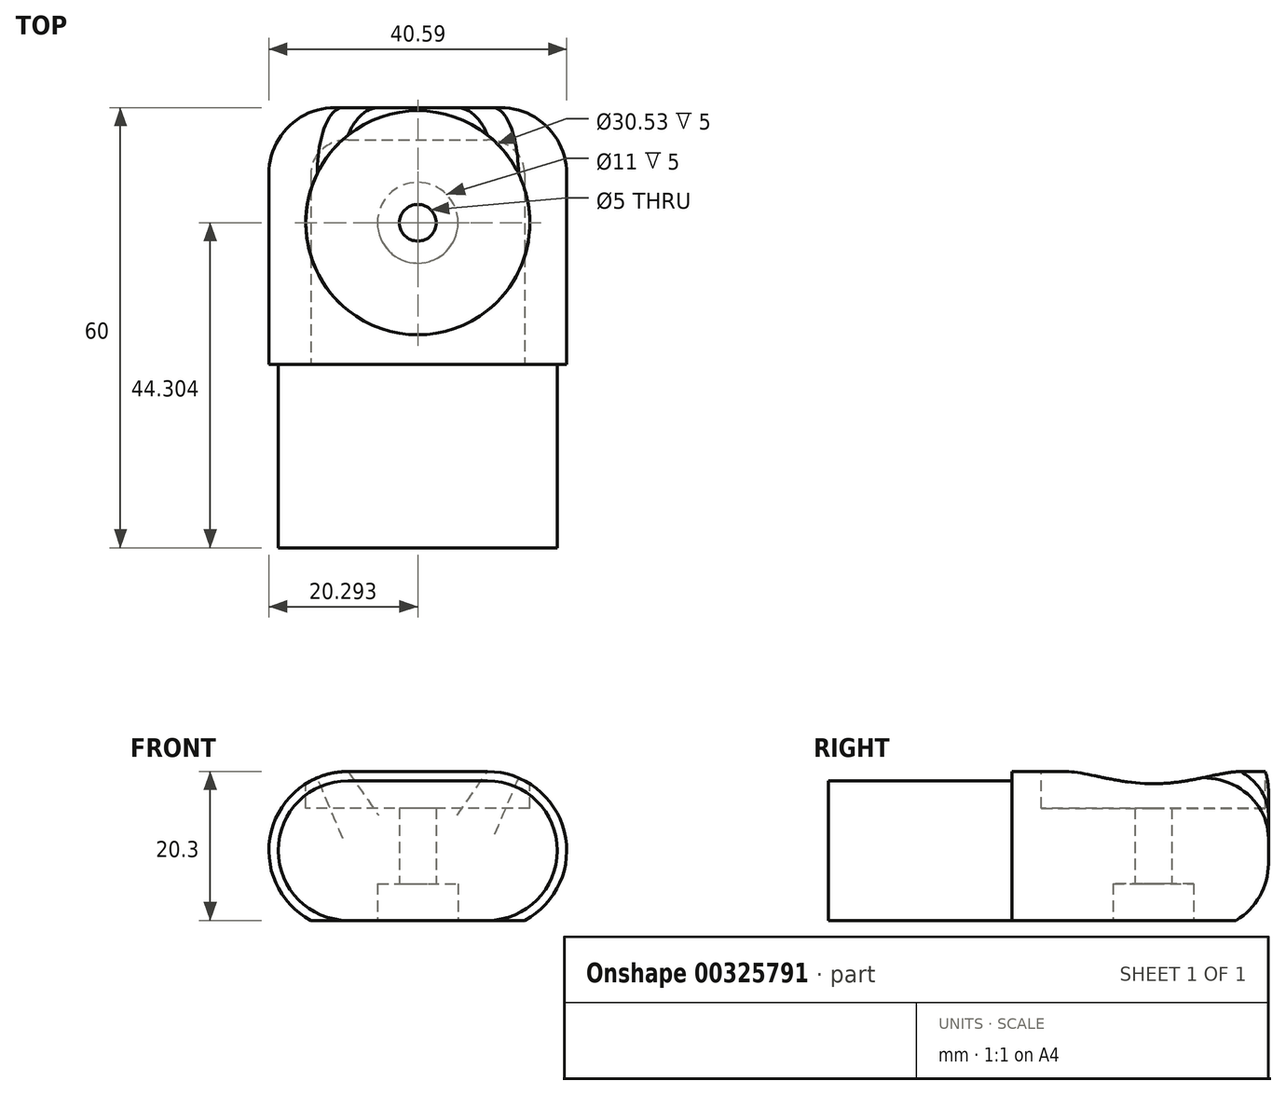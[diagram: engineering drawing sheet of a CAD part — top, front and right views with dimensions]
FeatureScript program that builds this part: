
annotation { "Feature Type Name" : "Feature", "Feature Type Description" : "" }
export const myFeature = defineFeature(function(context is Context, id is Id, definition is map)
    precondition{}
    {
        {
            var Q0;
            Q0=qCreatedBy(makeId("Front.planeOp"),FACE);
            var sketch = newSketch(context, id + "F0", { "sketchPlane" : qUnion([Q0])});
            skLineSegment(sketch, "E0", {"start": v(0, 9.52) * mm, "end": v(19.03, 9.52) * mm});
            skLineSegment(sketch, "E1", {"start": v(0, -9.52) * mm, "end": v(19.03, -9.52) * mm});
            skArc(sketch, "E2", {"start": v(0, 9.52) * mm, "mid": v(-9.52, 0) * mm, "end": v(0, -9.52) * mm});
            skArc(sketch, "E3", {"start": v(19.03, -9.52) * mm, "mid": v(28.54, 0) * mm, "end": v(19.03, 9.52) * mm});
            skSolve(sketch);
        }
        {
            var Q0;
            Q0=makeQuery(id+"F0.imprint","IMPRINT",FACE,{"disambiguationData":[TD([[makeQuery(id+"F0.imprint","IMPRINT",EDGE,{"derivedFrom":sQuery(id+"F0.wireOp",EDGE,"E0")}),-1.0]])]});
            extrude(context, id + "F1", {"entities" : qUnion([Q0]), "depth" : 25 * mm});
        }
        {
            var Q0;
            Q0=makeQuery(id+"F1.opExtrude","CAP_FACE",FACE,{"disambiguationData":[OSD([sQuery(id+"F0.wireOp",EDGE,"E0"),sQuery(id+"F0.wireOp",EDGE,"E1"),sQuery(id+"F0.wireOp",EDGE,"E2"),sQuery(id+"F0.wireOp",EDGE,"E3")])],"isStart":true});
            var sketch = newSketch(context, id + "F2", { "sketchPlane" : qUnion([Q0])});
            skLineSegment(sketch, "E4", {"start": v(0, -10.78) * mm, "end": v(-19.03, -10.78) * mm});
            skLineSegment(sketch, "E5", {"start": v(0, 10.78) * mm, "end": v(-19.03, 10.78) * mm});
            skArc(sketch, "E6", {"start": v(0, -10.78) * mm, "mid": v(10.78, 0) * mm, "end": v(0, 10.78) * mm});
            skArc(sketch, "E7", {"start": v(-19.03, 10.78) * mm, "mid": v(-29.8, 0) * mm, "end": v(-19.03, -10.78) * mm});
            skSolve(sketch);
        }
        {
            var Q0;
            Q0 = qSketchRegion(id + "F2", true);
            extrude(context, id + "F3", {"entities" : qUnion([Q0]), "operationType" : NewBodyOperationType.ADD, "depth" : 35 * mm});
        }
        {
            var Q0;
            Q0=makeQuery(id+"F3.opExtrude","SWEPT_FACE",FACE,{"disambiguationData":[OSD([sQuery(id+"F2.wireOp",EDGE,"E5")])]});
            var sketch = newSketch(context, id + "F4", { "sketchPlane" : qUnion([Q0])});
            skCircle(sketch, "E8", {"center": v(9.51, 19.3) * mm, "radius": 15.27 * mm});
            skSolve(sketch);
        }
        {
            var Q0;
            Q0 = qSketchRegion(id + "F4", true);
            var Q1;
            Q1=sQuery(id+"F4.wireOp",EDGE,"E8");
            extrude(context, id + "F5", {"entities" : qUnion([Q0]), "operationType" : NewBodyOperationType.REMOVE, "surfaceEntities" : qUnion([Q1]), "oppositeDirection" : true, "depth" : 5 * mm});
        }
        {
            var Q0;
            Q0=makeQuery(id+"F3.opExtrude","CAP_EDGE",EDGE,{"disambiguationData":[OSD([sQuery(id+"F2.wireOp",EDGE,"E6")])],"isStart":false});
            fillet(context, id + "F6", {"entities" : qUnion([Q0]), "radius" : 9 * mm, "tangentPropagation" : true, "allowEdgeOverflow" : false});
        }
        {
            var Q0;
            Q0=makeQuery(id+"F5.boolean.opBoolean","COPY",FACE,{"derivedFrom":makeQuery(id+"F5.opExtrude","CAP_FACE",FACE,{"disambiguationData":[OSD([sQuery(id+"F4.wireOp",EDGE,"E8")])],"isStart":false})});
            var sketch = newSketch(context, id + "F7", { "sketchPlane" : qUnion([Q0])});
            skPoint(sketch, "E9", {"position": v(9.51, 19.3) * mm});
            skLineSegment(sketch, "E10", {"start": v(9.51, 19.3) * mm, "end": v(9.51, 0) * mm});
            skCircle(sketch, "E11", {"center": v(9.51, 19.3) * mm, "radius": 2.05 * mm});
            skSolve(sketch);
        }
        {
            var Q0;
            Q0=makeQuery(id+"F3.opExtrude","SWEPT_FACE",FACE,{"disambiguationData":[OSD([sQuery(id+"F2.wireOp",EDGE,"E4")])]});
            var sketch = newSketch(context, id + "F8", { "sketchPlane" : qUnion([Q0])});
            skPoint(sketch, "E12", {"position": v(9.51, -19.3) * mm});
            skSolve(sketch);
        }
        {
            var Q0;
            Q0=makeQuery(id+"F3.opExtrude","CAP_FACE",FACE,{"disambiguationData":[OSD([sQuery(id+"F2.wireOp",EDGE,"E4"),sQuery(id+"F2.wireOp",EDGE,"E5"),sQuery(id+"F2.wireOp",EDGE,"E6"),sQuery(id+"F2.wireOp",EDGE,"E7")])],"isStart":true});
            var sketch = newSketch(context, id + "F9", { "sketchPlane" : qUnion([Q0])});
            skLineSegment(sketch, "E13", {"start": v(19.03, -9.52) * mm, "end": v(32.83, -9.52) * mm});
            skLineSegment(sketch, "E14", {"start": v(32.83, -9.52) * mm, "end": v(32.83, -13.22) * mm});
            skLineSegment(sketch, "E15", {"start": v(32.83, -13.22) * mm, "end": v(-13.64, -13.22) * mm});
            skLineSegment(sketch, "E16", {"start": v(-13.64, -13.22) * mm, "end": v(-13.64, -9.52) * mm});
            skLineSegment(sketch, "E17", {"start": v(-13.64, -9.52) * mm, "end": v(19.03, -9.52) * mm});
            skSolve(sketch);
        }
        {
            var Q0;
            {var subQ0=makeQuery(id+"F3.opExtrude","CAP_EDGE",EDGE,{"disambiguationData":[OSD([sQuery(id+"F2.wireOp",EDGE,"E4")])],"isStart":true});Q0=makeQuery(id+"F9.imprint","IMPRINT",FACE,{"disambiguationData":[TD([[makeQuery(id+"F9.imprint","IMPRINT",EDGE,{"derivedFrom":subQ0}),1.0]])]});}
            extrude(context, id + "F10", {"entities" : qUnion([Q0]), "operationType" : NewBodyOperationType.REMOVE, "oppositeDirection" : true, "depth" : 35 * mm});
        }
        {
            var Q0;
            Q0=sQuery(id+"F8.wireOp",VERTEX,"E12");
            var Q1;
            Q1=makeQuery(id+"F1.opExtrude","SWEPT_BODY",BODY,{"disambiguationData":[OSD([sQuery(id+"F0.wireOp",EDGE,"E0"),sQuery(id+"F0.wireOp",EDGE,"E1"),sQuery(id+"F0.wireOp",EDGE,"E2"),sQuery(id+"F0.wireOp",EDGE,"E3")])]});
            hole(context, id + "F11", {"style" : HoleStyle.C_BORE, "endStyle" : HoleEndStyle.THROUGH, "holeDiameter" : 5 * mm, "cBoreDiameter" : 11 * mm, "cBoreDepth" : 5 * mm, "tappedDepth" : 12 * mm, "tapClearance" : 3, "locations" : qUnion([Q0]), "scope" : qUnion([Q1])});
        }
    });
